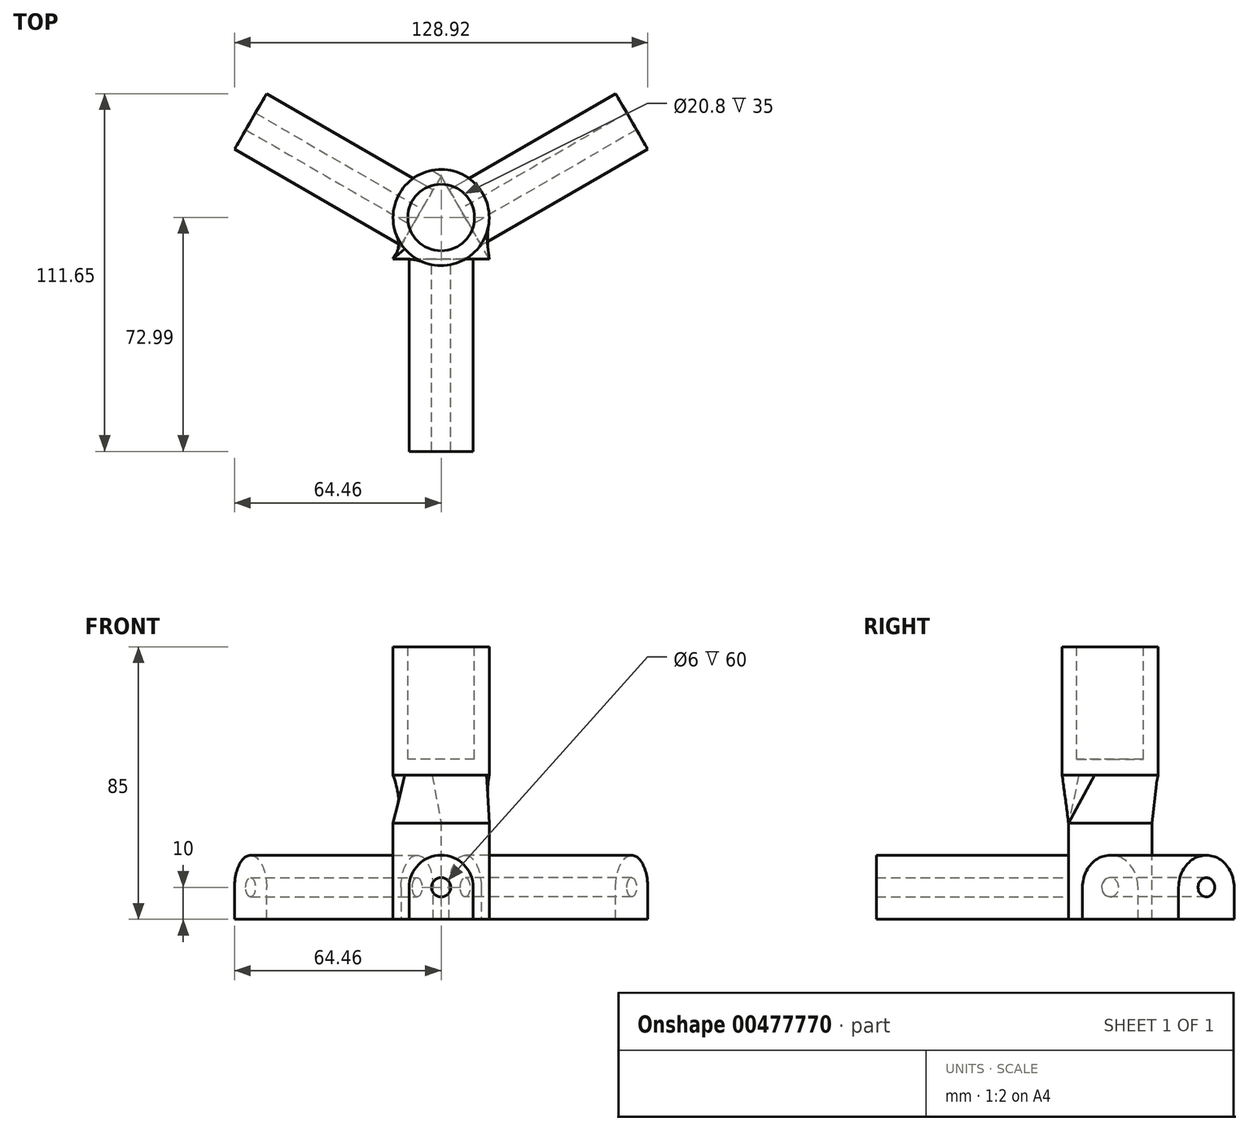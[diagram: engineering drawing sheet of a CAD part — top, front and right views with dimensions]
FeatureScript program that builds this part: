
annotation { "Feature Type Name" : "Feature", "Feature Type Description" : "" }
export const myFeature = defineFeature(function(context is Context, id is Id, definition is map)
    precondition{}
    {
        {
            var Q0;
            Q0=qCreatedBy(makeId("Top.planeOp"),FACE);
            var sketch = newSketch(context, id + "F0", { "sketchPlane" : qUnion([Q0])});
            skLineSegment(sketch, "E0", {"start": v(-15, 0) * mm, "end": v(15, 0) * mm});
            skLineSegment(sketch, "E1", {"start": v(15, 0) * mm, "end": v(0, 25.98) * mm});
            skLineSegment(sketch, "E2", {"start": v(0, 25.98) * mm, "end": v(-15, 0) * mm});
            skSolve(sketch);
        }
        {
            var Q0;
            Q0=makeQuery(id+"F0.imprint","IMPRINT",FACE,{"disambiguationData":[TD([[makeQuery(id+"F0.imprint","IMPRINT",EDGE,{"derivedFrom":sQuery(id+"F0.wireOp",EDGE,"E0")}),1.0]])]});
            extrude(context, id + "F1", {"entities" : qUnion([Q0]), "oppositeDirection" : true, "depth" : 30 * mm});
        }
        {
            var Q0;
            Q0=qCreatedBy(makeId("Right.planeOp"),FACE);
            var sketch = newSketch(context, id + "F2", { "sketchPlane" : qUnion([Q0])});
            skLineSegment(sketch, "E3", {"start": v(0, 0) * mm, "end": v(25.98, 0) * mm, "construction": true});
            skLineSegment(sketch, "E4", {"start": v(13, 0) * mm, "end": v(13, 15) * mm, "construction": true});
            skLineSegment(sketch, "E5", {"start": v(13, 0) * mm, "end": v(13, -36.27) * mm, "construction": true});
            skSolve(sketch);
        }
        {
            var Q0;
            Q0=makeQuery(id+"F1.opExtrude","CAP_FACE",FACE,{"disambiguationData":[OSD([sQuery(id+"F0.wireOp",EDGE,"E0"),sQuery(id+"F0.wireOp",EDGE,"E1"),sQuery(id+"F0.wireOp",EDGE,"E2")])],"isStart":true});
            cPlane(context, id + "F3", {"entities" : qUnion([Q0]), "cplaneType" : CPlaneType.OFFSET, "offset" : 15 * mm, "width" : 150 * mm, "height" : 150 * mm});
        }
        {
            var Q0;
            Q0=qCreatedBy(id+"F3.planeOp",FACE);
            var sketch = newSketch(context, id + "F4", { "sketchPlane" : qUnion([Q0])});
            skCircle(sketch, "E6", {"center": v(0, 13) * mm, "radius": 15 * mm});
            skSolve(sketch);
        }
        {
            var Q1;
            Q1=makeQuery(id+"F4.imprint","IMPRINT",FACE,{"disambiguationData":[TD([[makeQuery(id+"F4.imprint","IMPRINT",EDGE,{"derivedFrom":sQuery(id+"F4.wireOp",EDGE,"E6")}),1.0]])]});
            var Q2;
            Q2=makeQuery(id+"F1.opExtrude","CAP_FACE",FACE,{"disambiguationData":[OSD([sQuery(id+"F0.wireOp",EDGE,"E0"),sQuery(id+"F0.wireOp",EDGE,"E1"),sQuery(id+"F0.wireOp",EDGE,"E2")])],"isStart":true});
            loft(context, id + "F5", {"operationType" : NewBodyOperationType.ADD, "sheetProfilesArray" : [{ "sheetProfileEntities" : qUnion([Q1]) }, { "sheetProfileEntities" : qUnion([Q2]) }]});
        }
        {
            var Q0;
            Q0=makeQuery(id+"F5.opLoft","CAP_FACE",FACE,{"disambiguationData":[OSD([makeQuery(id+"F4.imprint","IMPRINT",FACE,{"disambiguationData":[TD([[makeQuery(id+"F4.imprint","IMPRINT",EDGE,{"derivedFrom":sQuery(id+"F4.wireOp",EDGE,"E6")}),1.0]])]})])],"isStart":true});
            extrude(context, id + "F6", {"entities" : qUnion([Q0]), "operationType" : NewBodyOperationType.ADD, "depth" : 40 * mm});
        }
        {
            var Q0;
            Q0=makeQuery(id+"F6.opExtrude","CAP_FACE",FACE,{"disambiguationData":[OSD([makeQuery(id+"F4.imprint","IMPRINT",FACE,{"disambiguationData":[TD([[makeQuery(id+"F4.imprint","IMPRINT",EDGE,{"derivedFrom":sQuery(id+"F4.wireOp",EDGE,"E6")}),1.0]])]})])],"isStart":false});
            var sketch = newSketch(context, id + "F7", { "sketchPlane" : qUnion([Q0])});
            skCircle(sketch, "E7", {"center": v(0, 13) * mm, "radius": 10.4 * mm});
            skSolve(sketch);
        }
        {
            var Q0;
            Q0 = qSketchRegion(id + "F7", true);
            extrude(context, id + "F8", {"entities" : qUnion([Q0]), "operationType" : NewBodyOperationType.REMOVE, "oppositeDirection" : true, "depth" : 35 * mm});
        }
        {
            var Q0;
            Q0=makeQuery(id+"F1.opExtrude","SWEPT_FACE",FACE,{"disambiguationData":[OSD([sQuery(id+"F0.wireOp",EDGE,"E0")])]});
            var sketch = newSketch(context, id + "F9", { "sketchPlane" : qUnion([Q0])});
            skLineSegment(sketch, "E8", {"start": v(0, 0) * mm, "end": v(0, -30) * mm, "construction": true});
            skArc(sketch, "E9", {"start": v(10, -20) * mm, "mid": v(0, -10) * mm, "end": v(-10, -20) * mm});
            skLineSegment(sketch, "E10", {"start": v(-10, -20) * mm, "end": v(-10, -30) * mm});
            skLineSegment(sketch, "E11", {"start": v(10, -20) * mm, "end": v(10, -30) * mm});
            skLineSegment(sketch, "E12", {"start": v(0, -20) * mm, "end": v(-15, -20) * mm, "construction": true});
            skLineSegment(sketch, "E13", {"start": v(-15, -20) * mm, "end": v(0, -20) * mm, "construction": true});
            skLineSegment(sketch, "E14", {"start": v(0, -20) * mm, "end": v(15, -20) * mm, "construction": true});
            skCircle(sketch, "E15", {"center": v(0, -20) * mm, "radius": 3 * mm});
            skSolve(sketch);
        }
        {
            var Q0;
            Q0=makeQuery(id+"F9.imprint","IMPRINT",FACE,{"disambiguationData":[TD([[makeQuery(id+"F9.imprint","IMPRINT",EDGE,{"derivedFrom":sQuery(id+"F9.wireOp",EDGE,"E9")}),1.0]])]});
            extrude(context, id + "F10", {"entities" : qUnion([Q0]), "operationType" : NewBodyOperationType.ADD, "depth" : 60 * mm});
        }
        {
            var Q0;
            {var subQ0=sQuery(id+"F0.wireOp",EDGE,"E0");Q0=makeQuery(id+"F10.boolean.opBoolean","MERGE",FACE,{"derivedFrom":[makeQuery(id+"F1.opExtrude","CAP_FACE",FACE,{"disambiguationData":[OSD([subQ0,sQuery(id+"F0.wireOp",EDGE,"E1"),sQuery(id+"F0.wireOp",EDGE,"E2")])],"isStart":false}),makeQuery(id+"F10.opExtrude","SWEPT_FACE",FACE,{"disambiguationData":[OSD([subQ0])]})]});}
            var sketch = newSketch(context, id + "F11", { "sketchPlane" : qUnion([Q0])});
            skLineSegment(sketch, "E16", {"start": v(0, 0) * mm, "end": v(0, -25.98) * mm, "construction": true});
            skSolve(sketch);
        }
        {
            var Q0;
            Q0=makeQuery(id+"F1.opExtrude","SWEPT_FACE",FACE,{"disambiguationData":[OSD([sQuery(id+"F0.wireOp",EDGE,"E1")])]});
            var sketch = newSketch(context, id + "F12", { "sketchPlane" : qUnion([Q0])});
            skLineSegment(sketch, "E17", {"start": v(7.5, -30) * mm, "end": v(7.5, 0) * mm, "construction": true});
            skPoint(sketch, "E18.middle", {"position": v(7.5, -30) * mm});
            skPoint(sketch, "E18.top.start.orphan", {"position": v(-2.5, -40) * mm});
            skPoint(sketch, "E19.orphan", {"position": v(17.5, -40) * mm});
            skLineSegment(sketch, "E20", {"start": v(7.5, -30) * mm, "end": v(17.5, -30) * mm});
            skLineSegment(sketch, "E21", {"start": v(17.5, -30) * mm, "end": v(17.5, -20) * mm});
            skLineSegment(sketch, "E22", {"start": v(-2.5, -20) * mm, "end": v(-2.5, -30) * mm});
            skLineSegment(sketch, "E23", {"start": v(-2.5, -30) * mm, "end": v(7.5, -30) * mm});
            skArc(sketch, "E24", {"start": v(17.5, -20) * mm, "mid": v(7.5, -10) * mm, "end": v(-2.5, -20) * mm});
            skCircle(sketch, "E25", {"center": v(7.5, -20) * mm, "radius": 3 * mm});
            skSolve(sketch);
        }
        {
            var Q0;
            Q0 = qSketchRegion(id + "F12", true);
            extrude(context, id + "F13", {"entities" : qUnion([Q0]), "operationType" : NewBodyOperationType.ADD, "depth" : 60 * mm});
        }
        {
            var Q0;
            Q0=makeQuery(id+"F1.opExtrude","SWEPT_FACE",FACE,{"disambiguationData":[OSD([sQuery(id+"F0.wireOp",EDGE,"E2")])]});
            var sketch = newSketch(context, id + "F14", { "sketchPlane" : qUnion([Q0])});
            skLineSegment(sketch, "E26", {"start": v(-7.5, -30) * mm, "end": v(-7.5, 0) * mm, "construction": true});
            skLineSegment(sketch, "E27", {"start": v(2.5, -30) * mm, "end": v(-17.5, -30) * mm});
            skLineSegment(sketch, "E28", {"start": v(-17.5, -30) * mm, "end": v(-17.5, -20) * mm});
            skLineSegment(sketch, "E29", {"start": v(2.5, -20) * mm, "end": v(2.5, -30) * mm});
            skArc(sketch, "E30", {"start": v(2.5, -20) * mm, "mid": v(-7.5, -10) * mm, "end": v(-17.5, -20) * mm});
            skCircle(sketch, "E31", {"center": v(-7.5, -20) * mm, "radius": 3 * mm});
            skSolve(sketch);
        }
        {
            var Q0;
            Q0=makeQuery(id+"F14.imprint","IMPRINT",FACE,{"disambiguationData":[TD([[makeQuery(id+"F14.imprint","IMPRINT",EDGE,{"derivedFrom":sQuery(id+"F14.wireOp",EDGE,"E27")}),1.0]])]});
            extrude(context, id + "F15", {"entities" : qUnion([Q0]), "operationType" : NewBodyOperationType.ADD, "depth" : 60 * mm});
        }
    });
